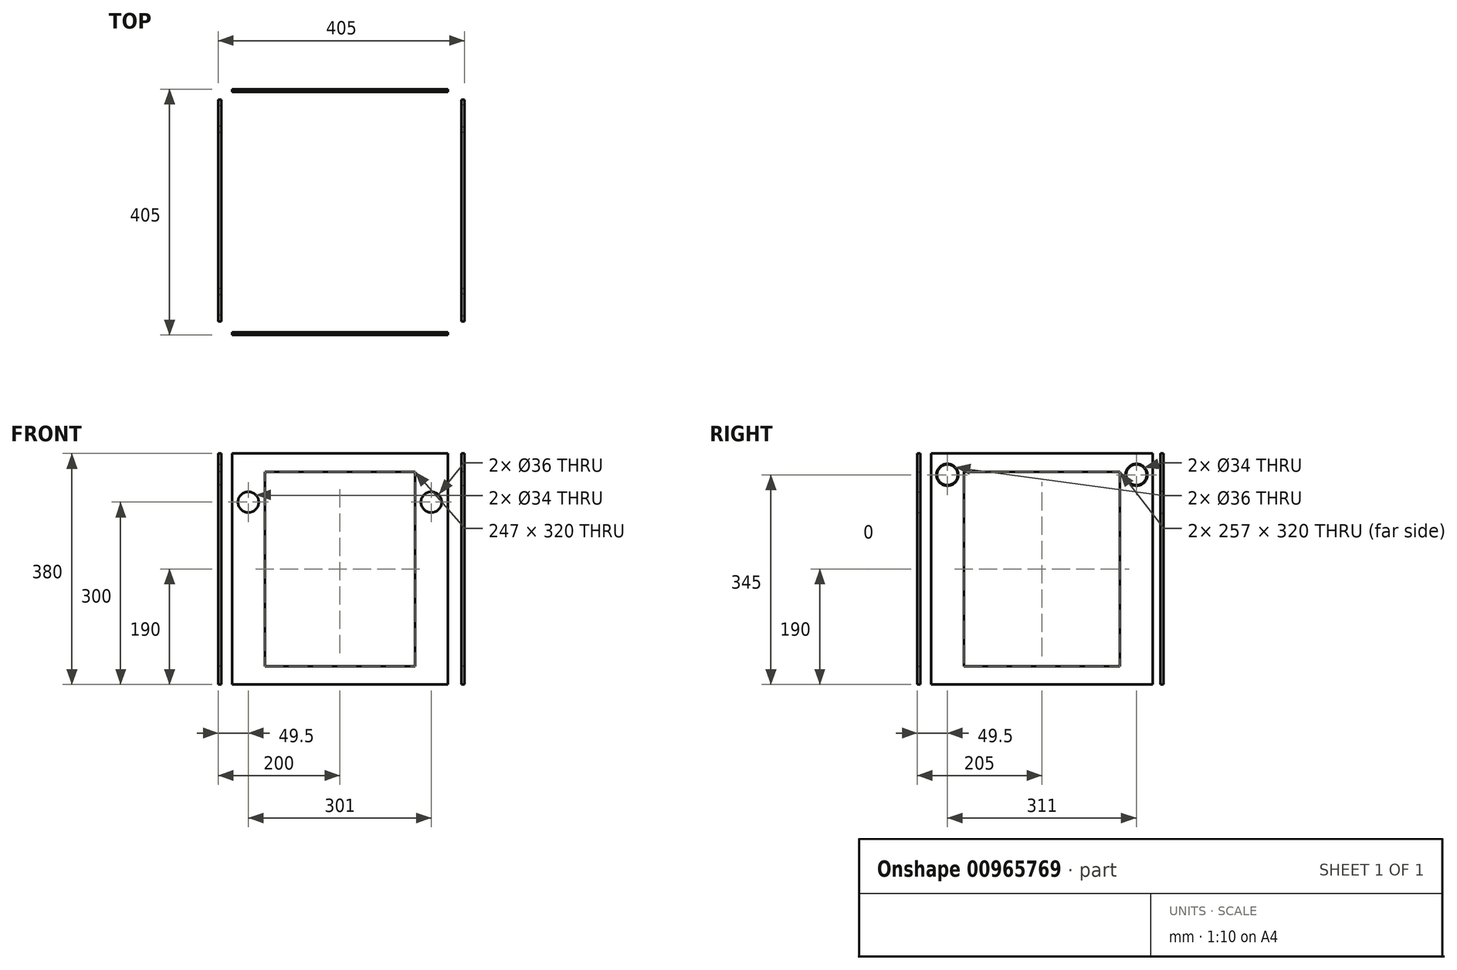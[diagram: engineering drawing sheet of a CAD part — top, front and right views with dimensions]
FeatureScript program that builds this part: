
annotation { "Feature Type Name" : "Feature", "Feature Type Description" : "" }
export const myFeature = defineFeature(function(context is Context, id is Id, definition is map)
    precondition{}
    {
        {
            var Q0;
            Q0=qCreatedBy(makeId("Front.planeOp"),FACE);
            cPlane(context, id + "F0", {"entities" : qUnion([Q0]), "cplaneType" : CPlaneType.OFFSET, "offset" : 200 * mm, "width" : 150 * mm, "height" : 150 * mm});
        }
        {
            var Q0;
            Q0=qCreatedBy(makeId("Front.planeOp"),FACE);
            cPlane(context, id + "F1", {"entities" : qUnion([Q0]), "cplaneType" : CPlaneType.OFFSET, "offset" : 200 * mm, "oppositeDirection" : true, "width" : 150 * mm, "height" : 150 * mm});
        }
        {
            var Q0;
            Q0=qCreatedBy(makeId("Right.planeOp"),FACE);
            cPlane(context, id + "F2", {"entities" : qUnion([Q0]), "cplaneType" : CPlaneType.OFFSET, "offset" : 200 * mm, "width" : 150 * mm, "height" : 150 * mm});
        }
        {
            var Q0;
            Q0=qCreatedBy(makeId("Right.planeOp"),FACE);
            cPlane(context, id + "F3", {"entities" : qUnion([Q0]), "cplaneType" : CPlaneType.OFFSET, "offset" : 200 * mm, "oppositeDirection" : true, "width" : 150 * mm, "height" : 150 * mm});
        }
        {
            assignVariable(context, id + "F4", {"name" : "Thickness", "anyValue" : 5});
        }
        {
            var Q0;
            Q0=qCreatedBy(id+"F2.planeOp",FACE);
            var sketch = newSketch(context, id + "F5", { "sketchPlane" : qUnion([Q0])});
            skLineSegment(sketch, "E0.bottom", {"start": v(182.5, -190) * mm, "end": v(-182.5, -190) * mm});
            skLineSegment(sketch, "E0.top", {"start": v(182.5, 190) * mm, "end": v(-182.5, 190) * mm});
            skLineSegment(sketch, "E0.left", {"start": v(182.5, -190) * mm, "end": v(182.5, 190) * mm});
            skLineSegment(sketch, "E0.right", {"start": v(-182.5, -190) * mm, "end": v(-182.5, 190) * mm});
            skPoint(sketch, "E0.middle", {"position": v(0, 0) * mm});
            skCircle(sketch, "E1", {"center": v(155.5, 155) * mm, "radius": 18 * mm});
            skCircle(sketch, "E2", {"center": v(-155.5, 155) * mm, "radius": 18 * mm});
            skLineSegment(sketch, "E3", {"start": v(-182.5, 68) * mm, "end": v(182.5, 68) * mm, "construction": true});
            skLineSegment(sketch, "E4.bottom", {"start": v(-128.5, 160) * mm, "end": v(128.5, 160) * mm});
            skLineSegment(sketch, "E4.top", {"start": v(-128.5, -160) * mm, "end": v(128.5, -160) * mm});
            skLineSegment(sketch, "E4.left", {"start": v(-128.5, 160) * mm, "end": v(-128.5, -160) * mm});
            skLineSegment(sketch, "E4.right", {"start": v(128.5, 160) * mm, "end": v(128.5, -160) * mm});
            skSolve(sketch);
        }
        {
            var Q0;
            Q0=qCreatedBy(id+"F1.planeOp",FACE);
            var sketch = newSketch(context, id + "F6", { "sketchPlane" : qUnion([Q0])});
            skLineSegment(sketch, "E5.bottom", {"start": v(-177.5, 190) * mm, "end": v(177.5, 190) * mm});
            skLineSegment(sketch, "E5.top", {"start": v(-177.5, -190) * mm, "end": v(177.5, -190) * mm});
            skLineSegment(sketch, "E5.left", {"start": v(-177.5, 190) * mm, "end": v(-177.5, -190) * mm});
            skLineSegment(sketch, "E5.right", {"start": v(177.5, 190) * mm, "end": v(177.5, -190) * mm});
            skCircle(sketch, "E6", {"center": v(150.5, 110) * mm, "radius": 18 * mm});
            skCircle(sketch, "E7", {"center": v(-150.5, 110) * mm, "radius": 18 * mm});
            skPoint(sketch, "E8.0", {"position": v(200, 190) * mm});
            skPoint(sketch, "E9.0", {"position": v(200, -190) * mm});
            skPoint(sketch, "E10", {"position": v(0, 190) * mm});
            skPoint(sketch, "E11.0", {"position": v(200, 155) * mm});
            skSolve(sketch);
        }
        {
            var Q0;
            Q0=qCreatedBy(id+"F0.planeOp",FACE);
            var sketch = newSketch(context, id + "F7", { "sketchPlane" : qUnion([Q0])});
            skLineSegment(sketch, "E12.0.0", {"start": v(-177.5, 190) * mm, "end": v(-177.5, -190) * mm});
            skLineSegment(sketch, "E12.0.1", {"start": v(-177.5, -190) * mm, "end": v(177.5, -190) * mm});
            skLineSegment(sketch, "E12.0.2", {"start": v(177.5, -190) * mm, "end": v(177.5, 190) * mm});
            skLineSegment(sketch, "E12.0.3", {"start": v(177.5, 190) * mm, "end": v(-177.5, 190) * mm});
            skPoint(sketch, "E13.0", {"position": v(-150.5, 110) * mm});
            skPoint(sketch, "E14.0", {"position": v(150.5, 110) * mm});
            skCircle(sketch, "E15", {"center": v(-150.5, 110) * mm, "radius": 17 * mm});
            skCircle(sketch, "E16", {"center": v(150.5, 110) * mm, "radius": 17 * mm});
            skLineSegment(sketch, "E17.bottom", {"start": v(-123.5, 160) * mm, "end": v(123.5, 160) * mm});
            skLineSegment(sketch, "E17.top", {"start": v(-123.5, -160) * mm, "end": v(123.5, -160) * mm});
            skLineSegment(sketch, "E17.left", {"start": v(-123.5, 160) * mm, "end": v(-123.5, -160) * mm});
            skLineSegment(sketch, "E17.right", {"start": v(123.5, 160) * mm, "end": v(123.5, -160) * mm});
            skSolve(sketch);
        }
        {
            var Q0;
            Q0=qCreatedBy(id+"F3.planeOp",FACE);
            var sketch = newSketch(context, id + "F8", { "sketchPlane" : qUnion([Q0])});
            skLineSegment(sketch, "E18.0.0", {"start": v(182.5, -190) * mm, "end": v(182.5, 190) * mm});
            skLineSegment(sketch, "E18.0.1", {"start": v(182.5, 190) * mm, "end": v(-182.5, 190) * mm});
            skLineSegment(sketch, "E18.0.2", {"start": v(-182.5, 190) * mm, "end": v(-182.5, -190) * mm});
            skLineSegment(sketch, "E18.0.3", {"start": v(-182.5, -190) * mm, "end": v(182.5, -190) * mm});
            skPoint(sketch, "E19.0", {"position": v(155.5, 155) * mm});
            skPoint(sketch, "E20.0", {"position": v(-155.5, 155) * mm});
            skCircle(sketch, "E21", {"center": v(155.5, 155) * mm, "radius": 17 * mm});
            skCircle(sketch, "E22", {"center": v(-155.5, 155) * mm, "radius": 17 * mm});
            skLineSegment(sketch, "E23.0.0", {"start": v(-128.5, 160) * mm, "end": v(-128.5, -160) * mm});
            skLineSegment(sketch, "E23.0.1", {"start": v(-128.5, -160) * mm, "end": v(128.5, -160) * mm});
            skLineSegment(sketch, "E23.0.2", {"start": v(128.5, -160) * mm, "end": v(128.5, 160) * mm});
            skLineSegment(sketch, "E23.0.3", {"start": v(128.5, 160) * mm, "end": v(-128.5, 160) * mm});
            skSolve(sketch);
        }
        {
            var Q0;
            Q0 = qSketchRegion(id + "F5", true);
            extrude(context, id + "F9", {"entities" : qUnion([Q0]), "depth" : (getVariable(context, 'Thickness')) * mm, "offsetDistance" : 25 * mm});
        }
        {
            var Q0;
            Q0 = qSketchRegion(id + "F6", true);
            extrude(context, id + "F10", {"entities" : qUnion([Q0]), "depth" : (getVariable(context, 'Thickness')) * mm, "offsetDistance" : 25 * mm});
        }
        {
            var Q0;
            Q0 = qSketchRegion(id + "F7", true);
            extrude(context, id + "F11", {"entities" : qUnion([Q0]), "depth" : (getVariable(context, 'Thickness')) * mm, "offsetDistance" : 25 * mm});
        }
        {
            var Q0;
            Q0 = qSketchRegion(id + "F8", true);
            extrude(context, id + "F12", {"entities" : qUnion([Q0]), "depth" : (getVariable(context, 'Thickness')) * mm, "offsetDistance" : 25 * mm});
        }
    });
